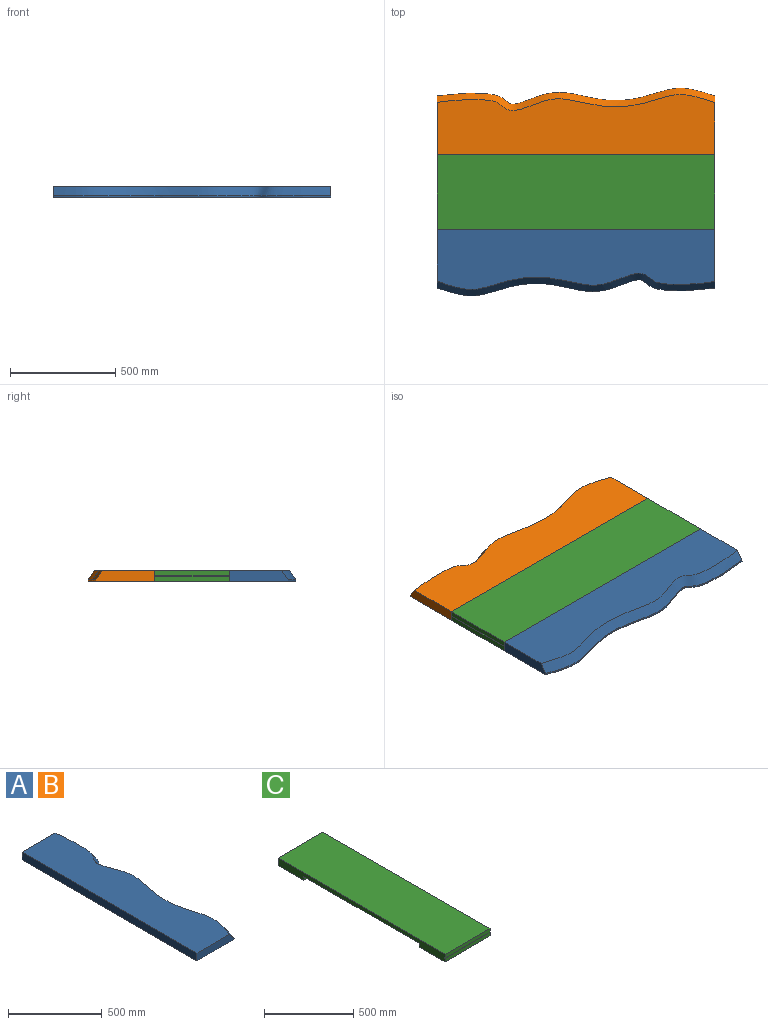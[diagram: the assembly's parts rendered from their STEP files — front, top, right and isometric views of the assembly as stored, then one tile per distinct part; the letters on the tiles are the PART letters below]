
ASSEMBLY  parts=3 mates=3
PART A: 7 faces, bbox 328.6x1367.1x53.2 mm
  f0: extruded ~1320.8x75.25mm, area 10351.8mm2, adj f1,f3,f5,f6
  f1: plane 279.4x50.8mm, normal (0,1,0), area 13531.1mm2, adj f0,f2,f4,f5,f6
  f2: plane 1320.8x50.8mm, normal (-1,0,0), area 67096.6mm2, adj f1,f3,f4,f5
  f3: plane 279.4x50.8mm, normal (0,-1,0), area 13505.1mm2, adj f0,f2,f4,f5,f6
  f4: plane 1323.15x288.42mm, normal (0,0,1), area 330948.6mm2, adj f1,f2,f3,f6
  f5: plane 1320.8x326.22mm, normal (0,0,-1), area 372577.3mm2, adj f0,f1,f2,f3
  f6: bspline ~1364.76x106.28mm, area 71605.4mm2, adj f0,f1,f3,f4
PART B: same geometry as A
PART C: 14 faces, bbox 355.6x1320.8x50.8 mm
  f0: plane 355.6x25mm, normal (0,-1,0), area 8891mm2, adj f1,f4,f8,f12
  f1: plane 1320.8x50.8mm, normal (1,0,0), area 43868.4mm2, adj f0,f2,f3,f5,f6,f7,f8,f9
  f2: plane 914.4x355.6mm, normal (0,0,-1), area 325160.6mm2, adj f1,f4,f7,f9
  f3: plane 355.6x50.8mm, normal (0,1,0), area 18064.5mm2, adj f1,f4,f6,f10
  f4: plane 1320.8x50.8mm, normal (-1,0,0), area 43868.4mm2, adj f0,f2,f3,f5,f6,f7,f8,f9
  f5: plane 355.6x25mm, normal (0,-1,0), area 8891mm2, adj f1,f4,f6,f11
  f6: plane 1320.8x355.6mm, normal (0,0,1), area 469676.5mm2, adj f1,f3,f4,f5
  f7: plane 355.6x25.4mm, normal (0,1,0), area 9032.2mm2, adj f1,f2,f4,f8
  f8: plane 355.6x203.2mm, normal (0,0,-1), area 72257.9mm2, adj f0,f1,f4,f7
  f9: plane 355.6x25.4mm, normal (0,-1,0), area 9032.2mm2, adj f1,f2,f4,f10
  f10: plane 355.6x203.2mm, normal (0,0,-1), area 72257.9mm2, adj f1,f3,f4,f9
  f11: plane 355.6x3.18mm, normal (0,0,-1), area 1129mm2, adj f1,f4,f5,f13
  f12: plane 355.6x3.18mm, normal (0,0,1), area 1129mm2, adj f0,f1,f4,f13
  f13: plane 355.6x0.79mm, normal (0,-1,0), area 282.5mm2, adj f1,f4,f11,f12
PLACE A rot(axis=(0,0,-1),90deg) t=(-696.85,-1023.7,-777.01)mm
PLACE B rot(axis=(0,0,1),90deg) t=(470.16,-109.3,-777.01)mm
PLACE C rot(axis=(0,0,-1),90deg) t=(-113.34,-566.5,-751.61)mm
MATE planar A.f4 <-> B.f4  axis (0,0,1) through (-121.26,-870.51,-726.21)mm
MATE fastened C.f6 <-> A.f4  axis (0,0,1) through (-113.34,-744.3,-726.21)mm
MATE fastened B.f4 <-> C.f6  axis (0,0,1) through (-113.34,-388.7,-726.21)mm
